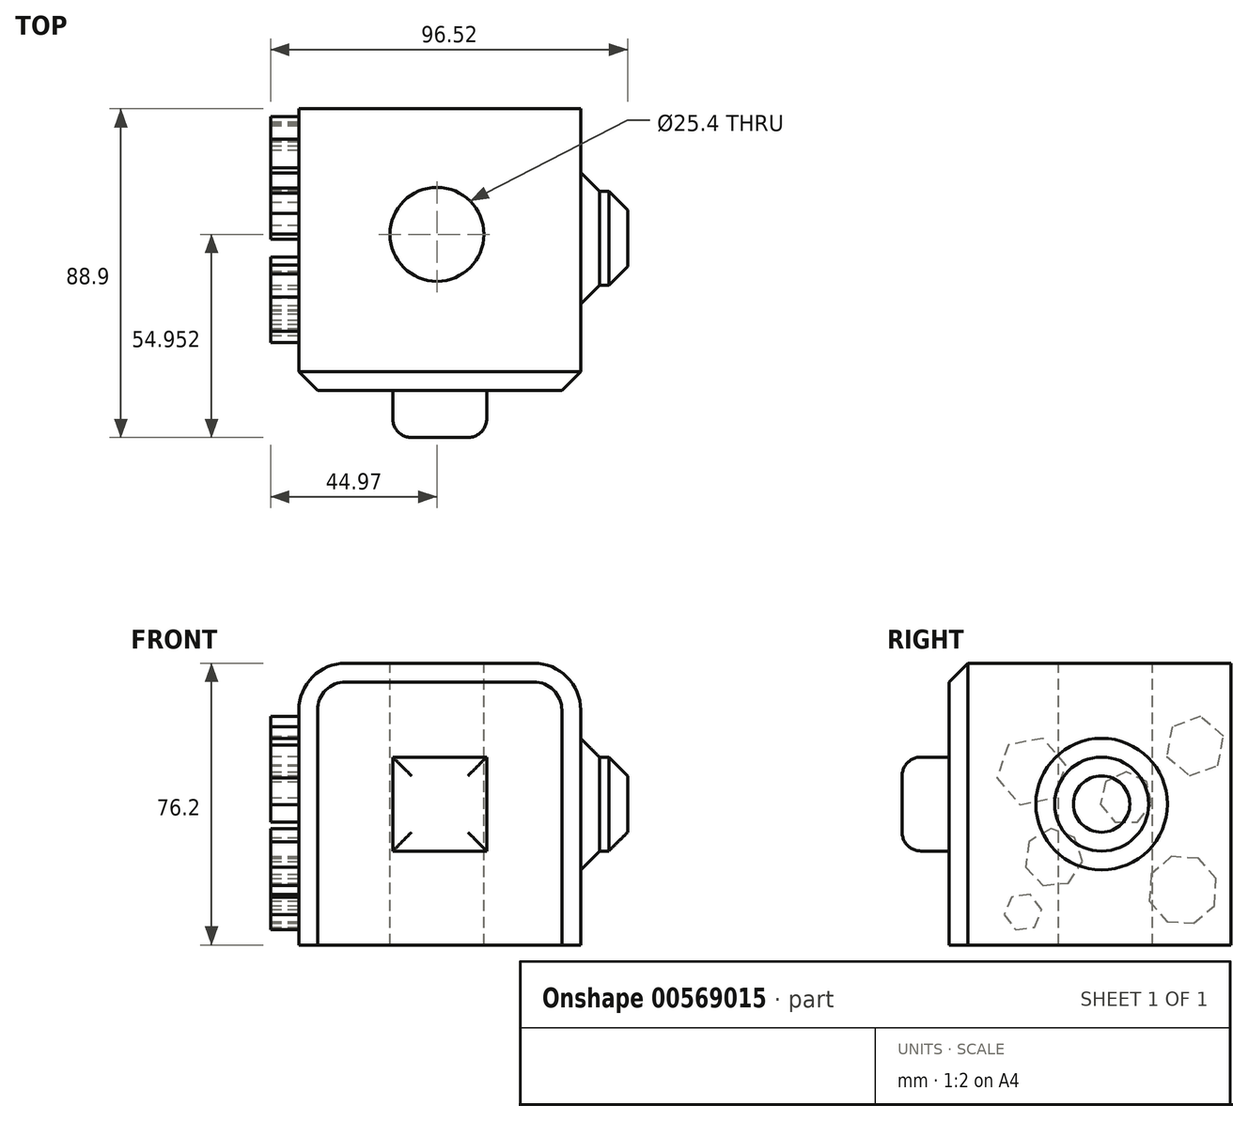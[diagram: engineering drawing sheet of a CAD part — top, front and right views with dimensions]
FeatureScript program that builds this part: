
annotation { "Feature Type Name" : "Feature", "Feature Type Description" : "" }
export const myFeature = defineFeature(function(context is Context, id is Id, definition is map)
    precondition{}
    {
        {
            var Q0;
            Q0=qCreatedBy(makeId("Front.planeOp"),FACE);
            var sketch = newSketch(context, id + "F0", { "sketchPlane" : qUnion([Q0])});
            skLineSegment(sketch, "E0.bottom", {"start": v(0, 0) * mm, "end": v(76.2, 0) * mm});
            skLineSegment(sketch, "E0.top", {"start": v(0, 76.2) * mm, "end": v(76.2, 76.2) * mm});
            skLineSegment(sketch, "E0.left", {"start": v(0, 0) * mm, "end": v(0, 76.2) * mm});
            skLineSegment(sketch, "E0.right", {"start": v(76.2, 0) * mm, "end": v(76.2, 76.2) * mm});
            skSolve(sketch);
        }
        {
            var Q0;
            Q0=makeQuery(id+"F0.imprint","IMPRINT",FACE,{"disambiguationData":[TD([[makeQuery(id+"F0.imprint","IMPRINT",EDGE,{"derivedFrom":sQuery(id+"F0.wireOp",EDGE,"E0.bottom")}),1.0]])]});
            extrude(context, id + "F1", {"entities" : qUnion([Q0]), "depth" : 76.2 * mm, "offsetDistance" : 25.4 * mm});
        }
        {
            var Q0;
            Q0=makeQuery(id+"F1.opExtrude","SWEPT_FACE",FACE,{"disambiguationData":[OSD([sQuery(id+"F0.wireOp",EDGE,"E0.top")])]});
            var sketch = newSketch(context, id + "F2", { "sketchPlane" : qUnion([Q0])});
            skPoint(sketch, "E1", {"position": v(37.35, -33.95) * mm});
            skSolve(sketch);
        }
        {
            var Q0;
            Q0=sQuery(id+"F2.wireOp",VERTEX,"E1");
            var Q1;
            Q1=makeQuery(id+"F1.opExtrude","SWEPT_BODY",BODY,{"disambiguationData":[OSD([sQuery(id+"F0.wireOp",EDGE,"E0.bottom"),sQuery(id+"F0.wireOp",EDGE,"E0.top"),sQuery(id+"F0.wireOp",EDGE,"E0.left"),sQuery(id+"F0.wireOp",EDGE,"E0.right")])]});
            hole(context, id + "F3", {"style" : HoleStyle.SIMPLE, "endStyle" : HoleEndStyle.THROUGH, "holeDiameter" : 25.4 * mm, "isTappedThrough" : true, "tappedDepth" : 12.7 * mm, "tapClearance" : 3, "locations" : qUnion([Q0]), "scope" : qUnion([Q1])});
        }
        {
            var Q0;
            Q0=makeQuery(id+"F1.opExtrude","CAP_FACE",FACE,{"disambiguationData":[OSD([sQuery(id+"F0.wireOp",EDGE,"E0.bottom"),sQuery(id+"F0.wireOp",EDGE,"E0.top"),sQuery(id+"F0.wireOp",EDGE,"E0.left"),sQuery(id+"F0.wireOp",EDGE,"E0.right")])],"isStart":false});
            var sketch = newSketch(context, id + "F4", { "sketchPlane" : qUnion([Q0])});
            skLineSegment(sketch, "E2.bottom", {"start": v(25.4, 50.8) * mm, "end": v(50.8, 50.8) * mm});
            skLineSegment(sketch, "E2.top", {"start": v(25.4, 25.4) * mm, "end": v(50.8, 25.4) * mm});
            skLineSegment(sketch, "E2.left", {"start": v(25.4, 50.8) * mm, "end": v(25.4, 25.4) * mm});
            skLineSegment(sketch, "E2.right", {"start": v(50.8, 50.8) * mm, "end": v(50.8, 25.4) * mm});
            skSolve(sketch);
        }
        {
            var Q0;
            Q0=makeQuery(id+"F4.imprint","IMPRINT",FACE,{"disambiguationData":[TD([[makeQuery(id+"F4.imprint","IMPRINT",EDGE,{"derivedFrom":sQuery(id+"F4.wireOp",EDGE,"E2.bottom")}),-1.0]])]});
            extrude(context, id + "F5", {"entities" : qUnion([Q0]), "operationType" : NewBodyOperationType.ADD, "depth" : 12.7 * mm, "offsetDistance" : 25.4 * mm});
        }
        {
            var Q0;
            Q0=makeQuery(id+"F1.opExtrude","SWEPT_FACE",FACE,{"disambiguationData":[OSD([sQuery(id+"F0.wireOp",EDGE,"E0.right")])]});
            var sketch = newSketch(context, id + "F6", { "sketchPlane" : qUnion([Q0])});
            skPoint(sketch, "E3", {"position": v(-34.96, 38.1) * mm});
            skCircle(sketch, "E4", {"center": v(-34.96, 38.1) * mm, "radius": 12.7 * mm});
            skSolve(sketch);
        }
        {
            var Q0;
            Q0=makeQuery(id+"F6.imprint","IMPRINT",FACE,{"disambiguationData":[TD([[makeQuery(id+"F6.imprint","IMPRINT",EDGE,{"derivedFrom":sQuery(id+"F6.wireOp",EDGE,"E4")}),1.0]])]});
            extrude(context, id + "F7", {"entities" : qUnion([Q0]), "operationType" : NewBodyOperationType.ADD, "depth" : 12.7 * mm, "offsetDistance" : 25.4 * mm});
        }
        {
            var Q0;
            Q0=makeQuery(id+"F1.opExtrude","SWEPT_EDGE",EDGE,{"disambiguationData":[OSD([sQuery(id+"F0.wireOp",EDGE,"E0.top"),sQuery(id+"F0.wireOp",EDGE,"E0.left")])]});
            fillet(context, id + "F8", {"entities" : qUnion([Q0]), "radius" : 12.7 * mm, "tangentPropagation" : true, "allowEdgeOverflow" : false});
        }
        {
            var Q0;
            Q0=makeQuery(id+"F1.opExtrude","SWEPT_EDGE",EDGE,{"disambiguationData":[OSD([sQuery(id+"F0.wireOp",EDGE,"E0.top"),sQuery(id+"F0.wireOp",EDGE,"E0.right")])]});
            fillet(context, id + "F9", {"entities" : qUnion([Q0]), "radius" : 12.7 * mm, "tangentPropagation" : true, "allowEdgeOverflow" : false});
        }
        {
            var Q0;
            Q0=makeQuery(id+"F1.opExtrude","CAP_EDGE",EDGE,{"disambiguationData":[OSD([sQuery(id+"F0.wireOp",EDGE,"E0.left")])],"isStart":false});
            chamfer(context, id + "F10", {"entities" : qUnion([Q0]), "width" : 5.08 * mm, "tangentPropagation" : true});
        }
        {
            var Q0;
            Q0=makeQuery(id+"F7.opExtrude","SWEPT_FACE",FACE,{"disambiguationData":[OSD([sQuery(id+"F6.wireOp",EDGE,"E4")])]});
            chamfer(context, id + "F11", {"entities" : qUnion([Q0]), "width" : 5.08 * mm, "tangentPropagation" : true});
        }
        {
            var Q0;
            Q0=makeQuery(id+"F5.opExtrude","CAP_FACE",FACE,{"disambiguationData":[OSD([sQuery(id+"F4.wireOp",EDGE,"E2.bottom"),sQuery(id+"F4.wireOp",EDGE,"E2.top"),sQuery(id+"F4.wireOp",EDGE,"E2.left"),sQuery(id+"F4.wireOp",EDGE,"E2.right")])],"isStart":false});
            fillet(context, id + "F12", {"entities" : qUnion([Q0]), "radius" : 5.08 * mm, "tangentPropagation" : true, "allowEdgeOverflow" : false});
        }
        {
            var Q0;
            Q0=makeQuery(id+"F1.opExtrude","SWEPT_FACE",FACE,{"disambiguationData":[OSD([sQuery(id+"F0.wireOp",EDGE,"E0.left")])]});
            var sketch = newSketch(context, id + "F13", { "sketchPlane" : qUnion([Q0])});
            skCircle(sketch, "E5.cCircle", {"center": v(28.32, 39.7) * mm, "radius": 6.4 * mm, "construction": true});
            skLineSegment(sketch, "E5.0", {"start": v(31.41, 33.29) * mm, "end": v(25.24, 33.29) * mm});
            skLineSegment(sketch, "E5.1", {"start": v(25.24, 33.29) * mm, "end": v(21.39, 38.11) * mm});
            skLineSegment(sketch, "E5.2", {"start": v(21.39, 38.11) * mm, "end": v(22.76, 44.13) * mm});
            skLineSegment(sketch, "E5.3", {"start": v(22.76, 44.13) * mm, "end": v(28.32, 46.8) * mm});
            skLineSegment(sketch, "E5.4", {"start": v(28.32, 46.8) * mm, "end": v(33.89, 44.13) * mm});
            skLineSegment(sketch, "E5.5", {"start": v(33.89, 44.13) * mm, "end": v(35.26, 38.11) * mm});
            skLineSegment(sketch, "E5.6", {"start": v(35.26, 38.11) * mm, "end": v(31.41, 33.29) * mm});
            skPoint(sketch, "E5.0.midPoint", {"position": v(28.32, 33.29) * mm});
            skSolve(sketch);
        }
        {
            var Q0;
            Q0=makeQuery(id+"F13.imprint","IMPRINT",FACE,{"disambiguationData":[TD([[makeQuery(id+"F13.imprint","IMPRINT",EDGE,{"derivedFrom":sQuery(id+"F13.wireOp",EDGE,"E5.0")}),-1.0]])]});
            extrude(context, id + "F14", {"entities" : qUnion([Q0]), "operationType" : NewBodyOperationType.ADD, "depth" : 7.62 * mm, "offsetDistance" : 25.4 * mm});
        }
        {
            var Q0;
            Q0=makeQuery(id+"F1.opExtrude","SWEPT_FACE",FACE,{"disambiguationData":[OSD([sQuery(id+"F0.wireOp",EDGE,"E0.left")])]});
            var sketch = newSketch(context, id + "F15", { "sketchPlane" : qUnion([Q0])});
            skCircle(sketch, "E6.cCircle", {"center": v(47.96, 23.57) * mm, "radius": 7.16 * mm, "construction": true});
            skLineSegment(sketch, "E6.0", {"start": v(55.52, 21.1) * mm, "end": v(50.74, 16.12) * mm});
            skLineSegment(sketch, "E6.1", {"start": v(50.74, 16.12) * mm, "end": v(43.87, 16.75) * mm});
            skLineSegment(sketch, "E6.2", {"start": v(43.87, 16.75) * mm, "end": v(40.08, 22.52) * mm});
            skLineSegment(sketch, "E6.3", {"start": v(40.08, 22.52) * mm, "end": v(42.23, 29.08) * mm});
            skLineSegment(sketch, "E6.4", {"start": v(42.23, 29.08) * mm, "end": v(48.7, 31.49) * mm});
            skLineSegment(sketch, "E6.5", {"start": v(48.7, 31.49) * mm, "end": v(54.61, 27.94) * mm});
            skLineSegment(sketch, "E6.6", {"start": v(54.61, 27.94) * mm, "end": v(55.52, 21.1) * mm});
            skPoint(sketch, "E6.0.midPoint", {"position": v(53.13, 18.6) * mm});
            skSolve(sketch);
        }
        {
            var Q0;
            Q0=makeQuery(id+"F15.imprint","IMPRINT",FACE,{"disambiguationData":[TD([[makeQuery(id+"F15.imprint","IMPRINT",EDGE,{"derivedFrom":sQuery(id+"F15.wireOp",EDGE,"E6.0")}),-1.0]])]});
            extrude(context, id + "F16", {"entities" : qUnion([Q0]), "operationType" : NewBodyOperationType.ADD, "depth" : 7.62 * mm, "offsetDistance" : 25.4 * mm});
        }
        {
            var Q0;
            Q0=makeQuery(id+"F1.opExtrude","SWEPT_FACE",FACE,{"disambiguationData":[OSD([sQuery(id+"F0.wireOp",EDGE,"E0.left")])]});
            var sketch = newSketch(context, id + "F17", { "sketchPlane" : qUnion([Q0])});
            skCircle(sketch, "E7.cCircle", {"center": v(53.96, 46.93) * mm, "radius": 8.2 * mm, "construction": true});
            skLineSegment(sketch, "E7.0", {"start": v(63.27, 45.14) * mm, "end": v(57.06, 37.97) * mm});
            skLineSegment(sketch, "E7.1", {"start": v(57.06, 37.97) * mm, "end": v(47.75, 39.77) * mm});
            skLineSegment(sketch, "E7.2", {"start": v(47.75, 39.77) * mm, "end": v(44.65, 48.73) * mm});
            skLineSegment(sketch, "E7.3", {"start": v(44.65, 48.73) * mm, "end": v(50.86, 55.89) * mm});
            skLineSegment(sketch, "E7.4", {"start": v(50.86, 55.89) * mm, "end": v(60.17, 54.1) * mm});
            skLineSegment(sketch, "E7.5", {"start": v(60.17, 54.1) * mm, "end": v(63.27, 45.14) * mm});
            skPoint(sketch, "E7.0.midPoint", {"position": v(60.16, 41.56) * mm});
            skSolve(sketch);
        }
        {
            var Q0;
            Q0=makeQuery(id+"F17.imprint","IMPRINT",FACE,{"disambiguationData":[TD([[makeQuery(id+"F17.imprint","IMPRINT",EDGE,{"derivedFrom":sQuery(id+"F17.wireOp",EDGE,"E7.0")}),-1.0]])]});
            extrude(context, id + "F18", {"entities" : qUnion([Q0]), "operationType" : NewBodyOperationType.ADD, "depth" : 7.62 * mm, "offsetDistance" : 25.4 * mm});
        }
        {
            var Q0;
            Q0=makeQuery(id+"F1.opExtrude","SWEPT_FACE",FACE,{"disambiguationData":[OSD([sQuery(id+"F0.wireOp",EDGE,"E0.left")])]});
            var sketch = newSketch(context, id + "F19", { "sketchPlane" : qUnion([Q0])});
            skCircle(sketch, "E8.cCircle", {"center": v(13.02, 14.89) * mm, "radius": 8.8 * mm, "construction": true});
            skLineSegment(sketch, "E8.0", {"start": v(22.04, 11.84) * mm, "end": v(17.24, 6.36) * mm});
            skLineSegment(sketch, "E8.1", {"start": v(17.24, 6.36) * mm, "end": v(9.98, 5.87) * mm});
            skLineSegment(sketch, "E8.2", {"start": v(9.98, 5.87) * mm, "end": v(4.5, 10.67) * mm});
            skLineSegment(sketch, "E8.3", {"start": v(4.5, 10.67) * mm, "end": v(4.01, 17.93) * mm});
            skLineSegment(sketch, "E8.4", {"start": v(4.01, 17.93) * mm, "end": v(8.8, 23.41) * mm});
            skLineSegment(sketch, "E8.5", {"start": v(8.8, 23.41) * mm, "end": v(16.07, 23.9) * mm});
            skLineSegment(sketch, "E8.6", {"start": v(16.07, 23.9) * mm, "end": v(21.55, 19.1) * mm});
            skLineSegment(sketch, "E8.7", {"start": v(21.55, 19.1) * mm, "end": v(22.04, 11.84) * mm});
            skPoint(sketch, "E8.0.midPoint", {"position": v(19.64, 9.1) * mm});
            skSolve(sketch);
        }
        {
            var Q0;
            Q0=makeQuery(id+"F19.imprint","IMPRINT",FACE,{"disambiguationData":[TD([[makeQuery(id+"F19.imprint","IMPRINT",EDGE,{"derivedFrom":sQuery(id+"F19.wireOp",EDGE,"E8.0")}),-1.0]])]});
            extrude(context, id + "F20", {"entities" : qUnion([Q0]), "operationType" : NewBodyOperationType.ADD, "depth" : 7.62 * mm, "offsetDistance" : 25.4 * mm});
        }
        {
            var Q0;
            Q0=makeQuery(id+"F1.opExtrude","SWEPT_FACE",FACE,{"disambiguationData":[OSD([sQuery(id+"F0.wireOp",EDGE,"E0.left")])]});
            var sketch = newSketch(context, id + "F21", { "sketchPlane" : qUnion([Q0])});
            skCircle(sketch, "E9.cCircle", {"center": v(9.72, 53.75) * mm, "radius": 7.04 * mm, "construction": true});
            skLineSegment(sketch, "E9.0", {"start": v(17.37, 51) * mm, "end": v(11.16, 45.75) * mm});
            skLineSegment(sketch, "E9.1", {"start": v(11.16, 45.75) * mm, "end": v(3.51, 48.5) * mm});
            skLineSegment(sketch, "E9.2", {"start": v(3.51, 48.5) * mm, "end": v(2.07, 56.5) * mm});
            skLineSegment(sketch, "E9.3", {"start": v(2.07, 56.5) * mm, "end": v(8.27, 61.75) * mm});
            skLineSegment(sketch, "E9.4", {"start": v(8.27, 61.75) * mm, "end": v(15.92, 59) * mm});
            skLineSegment(sketch, "E9.5", {"start": v(15.92, 59) * mm, "end": v(17.37, 51) * mm});
            skPoint(sketch, "E9.0.midPoint", {"position": v(14.27, 48.38) * mm});
            skSolve(sketch);
        }
        {
            var Q0;
            Q0=makeQuery(id+"F21.imprint","IMPRINT",FACE,{"disambiguationData":[TD([[makeQuery(id+"F21.imprint","IMPRINT",EDGE,{"derivedFrom":sQuery(id+"F21.wireOp",EDGE,"E9.0")}),-1.0]])]});
            extrude(context, id + "F22", {"entities" : qUnion([Q0]), "operationType" : NewBodyOperationType.ADD, "depth" : 7.62 * mm, "offsetDistance" : 25.4 * mm});
        }
        {
            var Q0;
            Q0=makeQuery(id+"F1.opExtrude","SWEPT_FACE",FACE,{"disambiguationData":[OSD([sQuery(id+"F0.wireOp",EDGE,"E0.left")])]});
            var sketch = newSketch(context, id + "F23", { "sketchPlane" : qUnion([Q0])});
            skCircle(sketch, "E10.cCircle", {"center": v(56.23, 8.9) * mm, "radius": 4.42 * mm, "construction": true});
            skLineSegment(sketch, "E10.0", {"start": v(61.3, 8.23) * mm, "end": v(58.2, 4.17) * mm});
            skLineSegment(sketch, "E10.1", {"start": v(58.2, 4.17) * mm, "end": v(53.13, 4.83) * mm});
            skLineSegment(sketch, "E10.2", {"start": v(53.13, 4.83) * mm, "end": v(51.17, 9.55) * mm});
            skLineSegment(sketch, "E10.3", {"start": v(51.17, 9.55) * mm, "end": v(54.27, 13.6) * mm});
            skLineSegment(sketch, "E10.4", {"start": v(54.27, 13.6) * mm, "end": v(59.34, 12.95) * mm});
            skLineSegment(sketch, "E10.5", {"start": v(59.34, 12.95) * mm, "end": v(61.3, 8.23) * mm});
            skPoint(sketch, "E10.0.midPoint", {"position": v(59.75, 6.2) * mm});
            skSolve(sketch);
        }
        {
            var Q0;
            Q0=makeQuery(id+"F23.imprint","IMPRINT",FACE,{"disambiguationData":[TD([[makeQuery(id+"F23.imprint","IMPRINT",EDGE,{"derivedFrom":sQuery(id+"F23.wireOp",EDGE,"E10.0")}),-1.0]])]});
            extrude(context, id + "F24", {"entities" : qUnion([Q0]), "operationType" : NewBodyOperationType.ADD, "depth" : 7.62 * mm, "offsetDistance" : 25.4 * mm});
        }
    });
